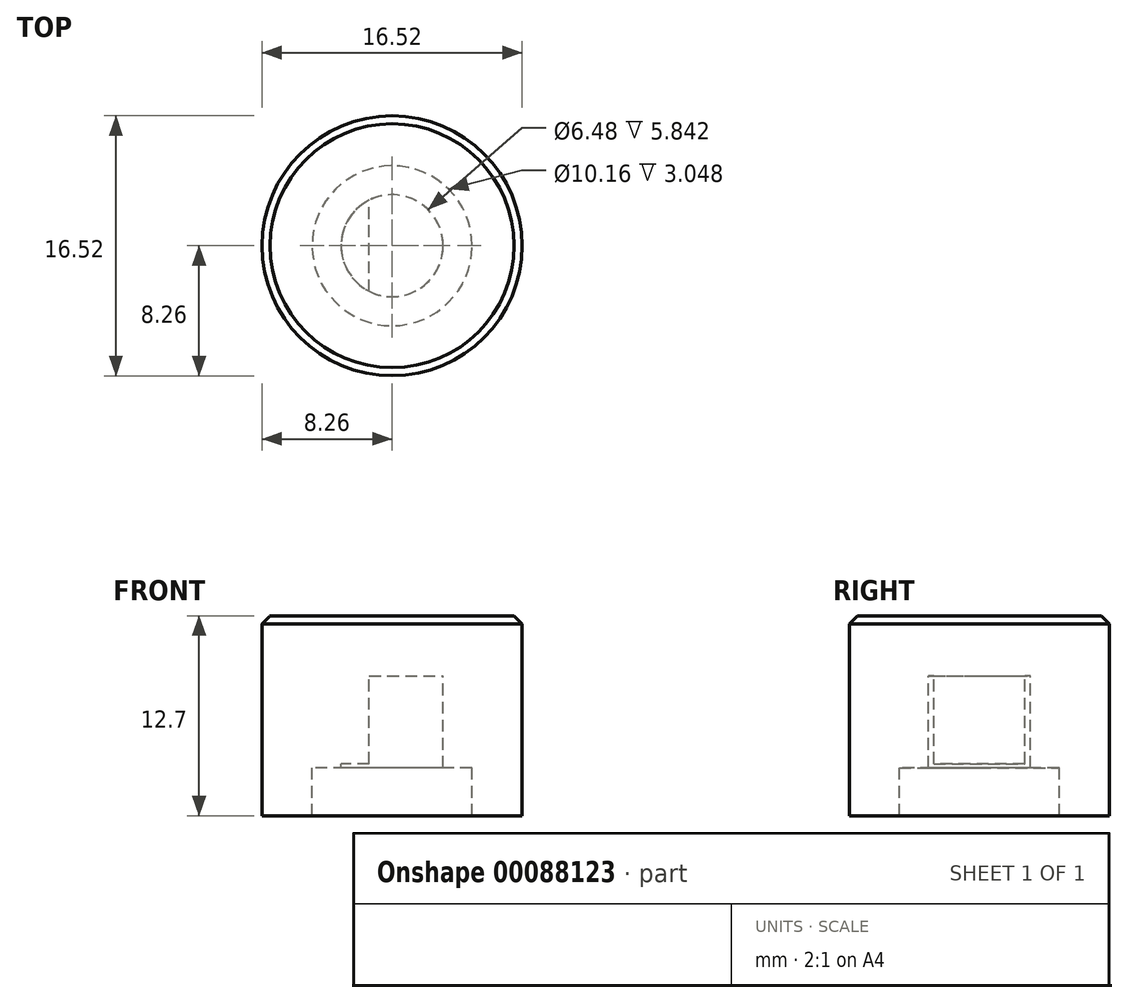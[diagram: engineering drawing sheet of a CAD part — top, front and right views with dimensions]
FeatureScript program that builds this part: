
annotation { "Feature Type Name" : "Feature", "Feature Type Description" : "" }
export const myFeature = defineFeature(function(context is Context, id is Id, definition is map)
    precondition{}
    {
        {
            var Q0;
            Q0=qCreatedBy(makeId("Front.planeOp"),FACE);
            var sketch = newSketch(context, id + "F0", { "sketchPlane" : qUnion([Q0])});
            skLineSegment(sketch, "E0", {"start": v(0, 5.84) * mm, "end": v(3.24, 5.84) * mm});
            skLineSegment(sketch, "E1", {"start": v(3.24, 5.84) * mm, "end": v(3.24, 0) * mm});
            skLineSegment(sketch, "E2", {"start": v(3.24, 0) * mm, "end": v(5.08, 0) * mm});
            skLineSegment(sketch, "E3", {"start": v(5.08, 0) * mm, "end": v(5.08, -3.05) * mm});
            skLineSegment(sketch, "E4", {"start": v(5.08, -3.05) * mm, "end": v(8.26, -3.05) * mm});
            skLineSegment(sketch, "E5", {"start": v(8.26, -3.05) * mm, "end": v(8.26, 9.65) * mm});
            skLineSegment(sketch, "E6", {"start": v(8.26, 9.65) * mm, "end": v(0, 9.65) * mm});
            skLineSegment(sketch, "E7", {"start": v(0, 9.65) * mm, "end": v(0, 5.84) * mm});
            skLineSegment(sketch, "E8.bottom", {"start": v(-4.5, 6.1) * mm, "end": v(-1.46, 6.1) * mm});
            skLineSegment(sketch, "E8.top", {"start": v(-4.5, 0.25) * mm, "end": v(-1.46, 0.25) * mm});
            skLineSegment(sketch, "E8.left", {"start": v(-4.5, 6.1) * mm, "end": v(-4.5, 0.25) * mm});
            skLineSegment(sketch, "E8.right", {"start": v(-1.46, 6.1) * mm, "end": v(-1.46, 0.25) * mm});
            skSolve(sketch);
        }
        {
            var Q0;
            Q0=makeQuery(id+"F0.imprint","IMPRINT",FACE,{"disambiguationData":[TD([[makeQuery(id+"F0.imprint","IMPRINT",EDGE,{"derivedFrom":sQuery(id+"F0.wireOp",EDGE,"E0")}),1.0]])]});
            var Q1;
            Q1=sQuery(id+"F0.wireOp",EDGE,"E7");
            revolve(context, id + "F1", {"entities" : qUnion([Q0]), "axis" : qUnion([Q1]), "revolveType" : RevolveType.FULL});
        }
        {
            var Q0;
            Q0=makeQuery(id+"F0.imprint","IMPRINT",FACE,{"disambiguationData":[TD([[makeQuery(id+"F0.imprint","IMPRINT",EDGE,{"derivedFrom":sQuery(id+"F0.wireOp",EDGE,"E8.bottom")}),-1.0]])]});
            extrude(context, id + "F2", {"entities" : qUnion([Q0]), "operationType" : NewBodyOperationType.ADD, "depth" : 7.62 * mm, "symmetric" : true});
        }
        {
            var Q0;
            Q0=makeQuery(id+"F1.opRevolve","SWEPT_EDGE",EDGE,{"disambiguationData":[OSD([sQuery(id+"F0.wireOp",EDGE,"E5"),sQuery(id+"F0.wireOp",EDGE,"E6")])]});
            chamfer(context, id + "F3", {"entities" : qUnion([Q0]), "width" : 0.5 * mm, "tangentPropagation" : true});
        }
    });
